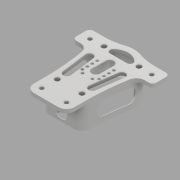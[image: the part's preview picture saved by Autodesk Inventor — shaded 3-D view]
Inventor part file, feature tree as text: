
AUTODESK INVENTOR PART (.ipt)
format: ipt  version: 2017 (Build 210142000, 142)  size: 713,216 bytes
history: native  units: mm
features: sketch x14, extrude x10, reference x8, fillet x5, hole x4, chamfer x3, projected_geometry x3, plane x2
ambient origin geometry x8: Origin, YZ Plane, XZ Plane, XY Plane, X Axis, Y Axis, Z Axis, Center Point
bodies: Solid1 (feature_tree)
feature tree (49):
  extrude  "Extrusion1"  Depth=10.0mm
  sketch  "Sketch2"  dims[d2=21.0mm d3=10.0mm]
  plane  "Work Plane1"
  extrude  "Extrusion2"  Depth=10.0mm
  extrude  "Extrusion4"  Depth=5.0mm TaperAngle=0.0deg
  fillet  "Fillet1"  Radius=1.0mm
  extrude  "Extrusion7"  Depth=3.5mm
  fillet  "Fillet3"  Radius=1.5mm
  extrude  "Extrusion8"  Depth=6.0mm
  extrude  "Extrusion9"  Depth=2.0mm
  fillet  "Fillet4"  Radius=3.5mm
  fillet  "Fillet5"  Radius=6.0mm
  fillet  "Fillet6"  Radius=1.5mm
  hole  "Hole1"  [1 undecoded]
  hole  "Hole2"  [1 undecoded]
  chamfer  "Chamfer1"  Distance=1.75mm Angle=45.0deg
  hole  "Hole3"  [1 undecoded]
  chamfer  "Chamfer2"  [1 undecoded]
  plane  "Work Plane4"
  extrude  "Extrusion10"  Depth=10.0mm
  chamfer  "Chamfer3"  Distance=3.0mm
  extrude  "Extrusion11"  Depth=10.0mm TaperAngle=45.0deg
  hole  "Hole4"  [1 undecoded]
  extrude  "Extrusion12"  Depth=10.0mm TaperAngle=0.0deg
  extrude  "Extrusion13"  Depth=10.0mm TaperAngle=0.0deg
  sketch  "Sketch1"  dims[d0=21.0mm d1=10.0mm]
  reference  "Reference2"
  reference  "Reference3"
  reference  "Reference4"
  reference  "Reference5"
  reference  "Reference6"
  reference  "Reference7"
  sketch  "Sketch4"  dims[d4=33.0mm d5=5.0mm d6=0.0mm d7=1.0mm]
  sketch  "Sketch7"  dims[d9=6.0mm d10=3.5mm d11=1.5mm]
  sketch  "Sketch8"  dims[d12=0.0mm d13=0.0mm d16=6.0mm]
  sketch  "Sketch10"  dims[d17=139.0mm d18=0.0mm d19=2.0mm d25=3.5mm d26=0.0mm d27=6.0mm d28=1.5mm d29=0.0mm]
  sketch  "Sketch11"  dims[d30=6.0mm d31=6.0mm]
  projected_geometry  "Projected Loop1"
  sketch  "Sketch12"  dims[d32=6.0mm d33=0.0mm d34=90.0mm]
  reference  "Reference10"
  sketch  "Sketch13"  dims[d35=13.75mm]
  reference  "Reference11"
  sketch  "Sketch16"  dims[d36=3.0mm]
  sketch  "Sketch17"  dims[d37=6.5mm d38=6.0mm d39=4.0mm d40=2.0mm d41=90.0deg d42=8.0mm d43=20.594885mm]
  projected_geometry  "Projected Loop2"
  sketch  "Sketch18"  dims[d44=100.0mm]
  sketch  "Sketch19"  dims[d45=108.0mm]
  projected_geometry  "Projected Loop3"
  sketch  "Sketch20"  dims[d46=4.5mm d47=6.0mm d48=8.0mm d49=10.0mm d50=90.0deg d51=8.0mm d52=20.594885mm d53=1.75mm d54=2.0mm d55=45.0deg d56=2.5mm d57=6.0mm d58=4.5mm d59=2.2mm d60=90.0deg d61=8.0mm d62=20.594885mm d63=1.0mm d64=2.0mm d65=45.0deg d66=-60.0mm d69=4.0mm d70=3.0mm d71=0.0mm d72=3.0mm d73=2.0mm d74=45.0deg d75=3.0mm d76=0.0mm d77=4.5mm d78=6.0mm d79=4.0mm d80=2.0mm d81=90.0deg d82=8.0mm d83=20.594885mm d84=10.0mm d85=0.0mm d86=10.0mm d87=0.0mm]
note: 5 required parameter values undecoded (feature->parameter linkage not recoverable at this tier; creation-order binding heuristic only, values carry confidence <= 0.55)
